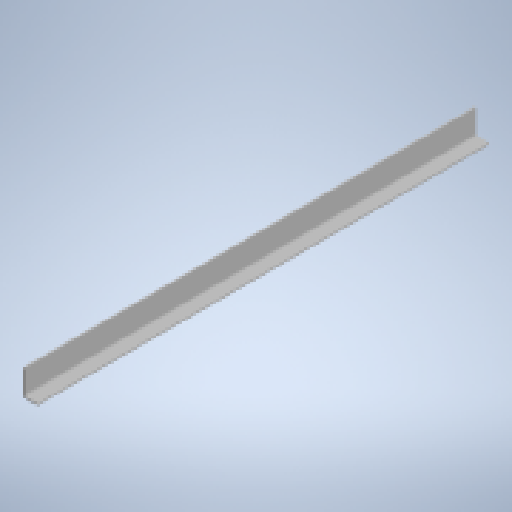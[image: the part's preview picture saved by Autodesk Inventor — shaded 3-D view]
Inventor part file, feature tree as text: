
AUTODESK INVENTOR PART (.ipt)
format: ipt  version: 2023 (Build 270158000, 158)  size: 141,312 bytes
history: native  units: in
note: dims shown in document units (in); Inventor stores cm internally (conversion verified against a paired STEP export)
features: extrude x1, sketch x1
ambient origin geometry x8: Origin, YZ Plane, XZ Plane, XY Plane, X Axis, Y Axis, Z Axis, Center Point
bodies: Solid1 (feature_tree)
feature tree (2):
  extrude  "Extrusion1"  Depth=1.75in
  sketch  "Sketch1"  dims[d0=0.188in d1=1.75in d2=3.0in d3=0.188in d4=53.0in d5=0.0in]
